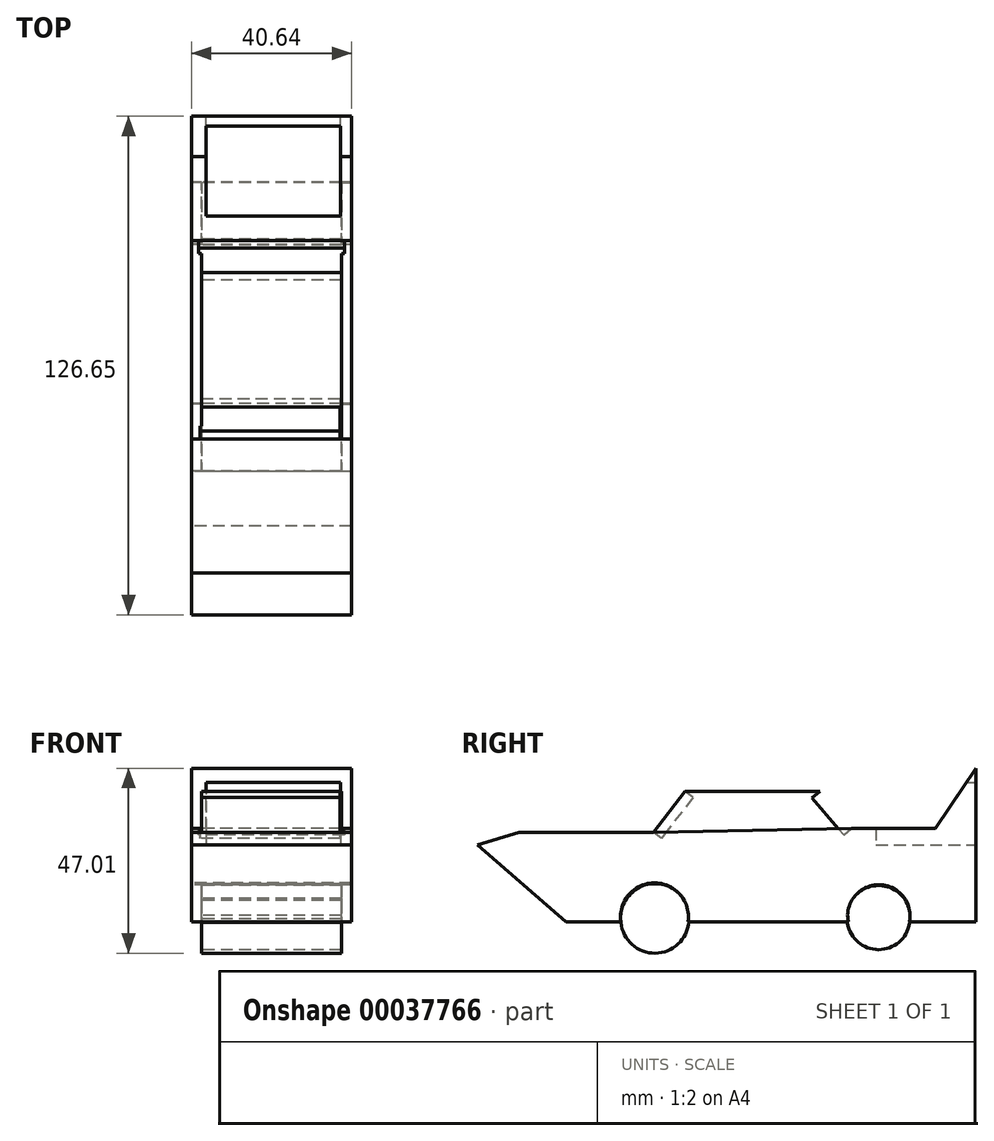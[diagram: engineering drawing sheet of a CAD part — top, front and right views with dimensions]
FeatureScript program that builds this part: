
annotation { "Feature Type Name" : "Feature", "Feature Type Description" : "" }
export const myFeature = defineFeature(function(context is Context, id is Id, definition is map)
    precondition{}
    {
        {
            var Q0;
            Q0=qCreatedBy(makeId("Right.planeOp"),FACE);
            var sketch = newSketch(context, id + "F0", { "sketchPlane" : qUnion([Q0])});
            skLineSegment(sketch, "E0", {"start": v(53.34, 19.52) * mm, "end": v(53.34, -19.52) * mm});
            skLineSegment(sketch, "E1", {"start": v(53.34, -19.52) * mm, "end": v(36.48, -19.52) * mm});
            skArc(sketch, "E2", {"start": v(36.48, -19.52) * mm, "mid": v(28.69, -10.07) * mm, "end": v(20.9, -19.52) * mm});
            skLineSegment(sketch, "E3", {"start": v(20.9, -19.52) * mm, "end": v(-19.8, -19.52) * mm});
            skArc(sketch, "E4", {"start": v(-19.8, -19.52) * mm, "mid": v(-28.32, -9.6) * mm, "end": v(-36.84, -19.52) * mm});
            skLineSegment(sketch, "E5", {"start": v(-36.84, -19.52) * mm, "end": v(-50.75, -19.52) * mm});
            skLineSegment(sketch, "E6", {"start": v(-50.75, -19.52) * mm, "end": v(-73.31, 0) * mm});
            skLineSegment(sketch, "E7", {"start": v(-73.31, 0) * mm, "end": v(-62.74, 3.2) * mm});
            skLineSegment(sketch, "E8", {"start": v(-62.74, 3.2) * mm, "end": v(-28.63, 3.2) * mm});
            skLineSegment(sketch, "E9", {"start": v(-28.63, 3.2) * mm, "end": v(-20.56, 13.66) * mm});
            skLineSegment(sketch, "E10", {"start": v(-20.56, 13.66) * mm, "end": v(13.66, 13.66) * mm});
            skLineSegment(sketch, "E11", {"start": v(13.66, 13.66) * mm, "end": v(21.73, 4.17) * mm});
            skLineSegment(sketch, "E12", {"start": v(21.73, 4.17) * mm, "end": v(43.09, 4.17) * mm});
            skLineSegment(sketch, "E13", {"start": v(43.09, 4.17) * mm, "end": v(53.34, 19.52) * mm});
            skArc(sketch, "E14", {"start": v(20.9, -19.52) * mm, "mid": v(28.69, -25.79) * mm, "end": v(36.48, -19.52) * mm});
            skArc(sketch, "E15", {"start": v(-36.84, -19.52) * mm, "mid": v(-28.32, -26.78) * mm, "end": v(-19.8, -19.52) * mm});
            skLineSegment(sketch, "E16", {"start": v(21.73, 4.17) * mm, "end": v(-28.63, 3.2) * mm});
            skSolve(sketch);
        }
        {
            var Q0;
            Q0=makeQuery(id+"F0.imprint","IMPRINT",FACE,{"disambiguationData":[TD([[makeQuery(id+"F0.imprint","IMPRINT",EDGE,{"derivedFrom":sQuery(id+"F0.wireOp",EDGE,"E9")}),-1.0]])]});
            var Q1;
            Q1=makeQuery(id+"F0.imprint","IMPRINT",FACE,{"disambiguationData":[TD([[makeQuery(id+"F0.imprint","IMPRINT",EDGE,{"derivedFrom":sQuery(id+"F0.wireOp",EDGE,"E0")}),-1.0]])]});
            extrude(context, id + "F1", {"entities" : qUnion([Q0, Q1]), "depth" : 45.72 * mm});
        }
        {
            var Q0;
            Q0=qCreatedBy(makeId("Right.planeOp"),FACE);
            var sketch = newSketch(context, id + "F2", { "sketchPlane" : qUnion([Q0])});
            skArc(sketch, "E17", {"start": v(36.48, -19.89) * mm, "mid": v(28.6, -10.28) * mm, "end": v(20.71, -19.89) * mm});
            skArc(sketch, "E18", {"start": v(20.71, -19.89) * mm, "mid": v(28.6, -26.57) * mm, "end": v(36.48, -19.89) * mm});
            skArc(sketch, "E19", {"start": v(-19.61, -19.52) * mm, "mid": v(-28.33, -9.81) * mm, "end": v(-36.84, -19.7) * mm});
            skArc(sketch, "E20", {"start": v(-36.84, -19.7) * mm, "mid": v(-28.14, -27.49) * mm, "end": v(-19.61, -19.52) * mm});
            skSolve(sketch);
        }
        {
            var Q0;
            Q0=makeQuery(id+"F2.imprint","IMPRINT",FACE,{"disambiguationData":[TD([[makeQuery(id+"F2.imprint","IMPRINT",EDGE,{"derivedFrom":sQuery(id+"F2.wireOp",EDGE,"E17")}),1.0]])]});
            var Q1;
            Q1=makeQuery(id+"F2.imprint","IMPRINT",FACE,{"disambiguationData":[TD([[makeQuery(id+"F2.imprint","IMPRINT",EDGE,{"derivedFrom":sQuery(id+"F2.wireOp",EDGE,"E19")}),1.0]])]});
            extrude(context, id + "F3", {"entities" : qUnion([Q0, Q1]), "operationType" : NewBodyOperationType.ADD, "depth" : 40.64 * mm});
        }
        {
            var Q0;
            Q0=makeQuery(id+"F1.opExtrude","SWEPT_BODY",BODY,{"disambiguationData":[OSD([sQuery(id+"F0.wireOp",EDGE,"E0"),sQuery(id+"F0.wireOp",EDGE,"E1"),sQuery(id+"F0.wireOp",EDGE,"E2"),sQuery(id+"F0.wireOp",EDGE,"E3"),sQuery(id+"F0.wireOp",EDGE,"E4"),sQuery(id+"F0.wireOp",EDGE,"E5"),sQuery(id+"F0.wireOp",EDGE,"E6"),sQuery(id+"F0.wireOp",EDGE,"E7"),sQuery(id+"F0.wireOp",EDGE,"E8"),sQuery(id+"F0.wireOp",EDGE,"E9"),sQuery(id+"F0.wireOp",EDGE,"E10"),sQuery(id+"F0.wireOp",EDGE,"E11"),sQuery(id+"F0.wireOp",EDGE,"E12"),sQuery(id+"F0.wireOp",EDGE,"E13")])]});
            var Q1;
            Q1=qCreatedBy(makeId("Right.planeOp"),FACE);
            mirror(context, id + "F4", {"operationType" : NewBodyOperationType.ADD, "entities" : qUnion([Q0]), "mirrorPlane" : qUnion([Q1])});
        }
        {
            var Q0;
            Q0=makeQuery(id+"F1.opExtrude","CAP_FACE",FACE,{"disambiguationData":[OSD([sQuery(id+"F0.wireOp",EDGE,"E0"),sQuery(id+"F0.wireOp",EDGE,"E1"),sQuery(id+"F0.wireOp",EDGE,"E2"),sQuery(id+"F0.wireOp",EDGE,"E3"),sQuery(id+"F0.wireOp",EDGE,"E4"),sQuery(id+"F0.wireOp",EDGE,"E5"),sQuery(id+"F0.wireOp",EDGE,"E6"),sQuery(id+"F0.wireOp",EDGE,"E7"),sQuery(id+"F0.wireOp",EDGE,"E8"),sQuery(id+"F0.wireOp",EDGE,"E9"),sQuery(id+"F0.wireOp",EDGE,"E10"),sQuery(id+"F0.wireOp",EDGE,"E11"),sQuery(id+"F0.wireOp",EDGE,"E12"),sQuery(id+"F0.wireOp",EDGE,"E13")])],"isStart":false});
            var Q1;
            Q1=makeQuery(id+"F3.opExtrude","CAP_FACE",FACE,{"disambiguationData":[OSD([sQuery(id+"F2.wireOp",EDGE,"E19"),sQuery(id+"F2.wireOp",EDGE,"E20")])],"isStart":false});
            extrude(context, id + "F5", {"entities" : qUnion([Q0, Q1]), "operationType" : NewBodyOperationType.REMOVE, "oppositeDirection" : true, "depth" : 25.4 * mm});
        }
        {
            var Q0;
            Q0=makeQuery(id+"F3.opExtrude","CAP_FACE",FACE,{"disambiguationData":[OSD([sQuery(id+"F2.wireOp",EDGE,"E17"),sQuery(id+"F2.wireOp",EDGE,"E18")])],"isStart":false});
            extrude(context, id + "F6", {"entities" : qUnion([Q0]), "operationType" : NewBodyOperationType.REMOVE, "oppositeDirection" : true, "depth" : 25.4 * mm});
        }
        {
            var Q0;
            Q0=makeQuery(id+"F4.opPattern","COPY",FACE,{"derivedFrom":makeQuery(id+"F1.opExtrude","CAP_FACE",FACE,{"disambiguationData":[OSD([sQuery(id+"F0.wireOp",EDGE,"E0"),sQuery(id+"F0.wireOp",EDGE,"E1"),sQuery(id+"F0.wireOp",EDGE,"E2"),sQuery(id+"F0.wireOp",EDGE,"E3"),sQuery(id+"F0.wireOp",EDGE,"E4"),sQuery(id+"F0.wireOp",EDGE,"E5"),sQuery(id+"F0.wireOp",EDGE,"E6"),sQuery(id+"F0.wireOp",EDGE,"E7"),sQuery(id+"F0.wireOp",EDGE,"E8"),sQuery(id+"F0.wireOp",EDGE,"E9"),sQuery(id+"F0.wireOp",EDGE,"E10"),sQuery(id+"F0.wireOp",EDGE,"E11"),sQuery(id+"F0.wireOp",EDGE,"E12"),sQuery(id+"F0.wireOp",EDGE,"E13")])],"isStart":false}),"instanceName":"1"});
            extrude(context, id + "F7", {"entities" : qUnion([Q0]), "operationType" : NewBodyOperationType.REMOVE, "oppositeDirection" : true, "depth" : 25.4 * mm});
        }
        {
            var Q0;
            Q0=makeQuery(id+"F4.opPattern","COPY",FACE,{"derivedFrom":makeQuery(id+"F3.opExtrude","CAP_FACE",FACE,{"disambiguationData":[OSD([sQuery(id+"F2.wireOp",EDGE,"E17"),sQuery(id+"F2.wireOp",EDGE,"E18")])],"isStart":false}),"instanceName":"1"});
            var Q1;
            Q1=makeQuery(id+"F4.opPattern","COPY",FACE,{"derivedFrom":makeQuery(id+"F3.opExtrude","CAP_FACE",FACE,{"disambiguationData":[OSD([sQuery(id+"F2.wireOp",EDGE,"E19"),sQuery(id+"F2.wireOp",EDGE,"E20")])],"isStart":false}),"instanceName":"1"});
            extrude(context, id + "F8", {"entities" : qUnion([Q0, Q1]), "operationType" : NewBodyOperationType.REMOVE, "oppositeDirection" : true, "depth" : 25.4 * mm});
        }
        {
            var Q0;
            Q0=makeQuery(id+"F5.boolean.opBoolean","COPY",FACE,{"derivedFrom":makeQuery(id+"F5.opExtrude","CAP_FACE",FACE,{"disambiguationData":[OSD([sQuery(id+"F2.wireOp",EDGE,"E19"),sQuery(id+"F2.wireOp",EDGE,"E20")])],"isStart":false})});
            var Q1;
            Q1=makeQuery(id+"F6.boolean.opBoolean","COPY",FACE,{"derivedFrom":makeQuery(id+"F6.opExtrude","CAP_FACE",FACE,{"disambiguationData":[OSD([sQuery(id+"F2.wireOp",EDGE,"E17"),sQuery(id+"F2.wireOp",EDGE,"E18")])],"isStart":false})});
            extrude(context, id + "F9", {"entities" : qUnion([Q0, Q1]), "operationType" : NewBodyOperationType.ADD, "depth" : 2.54 * mm});
        }
        {
            var Q0;
            Q0=makeQuery(id+"F8.boolean.opBoolean","COPY",FACE,{"derivedFrom":makeQuery(id+"F8.opExtrude","CAP_FACE",FACE,{"disambiguationData":[OSD([sQuery(id+"F2.wireOp",EDGE,"E17"),sQuery(id+"F2.wireOp",EDGE,"E18")])],"isStart":false})});
            var Q1;
            Q1=makeQuery(id+"F8.boolean.opBoolean","COPY",FACE,{"derivedFrom":makeQuery(id+"F8.opExtrude","CAP_FACE",FACE,{"disambiguationData":[OSD([sQuery(id+"F2.wireOp",EDGE,"E19"),sQuery(id+"F2.wireOp",EDGE,"E20")])],"isStart":false})});
            extrude(context, id + "F10", {"entities" : qUnion([Q0, Q1]), "operationType" : NewBodyOperationType.ADD, "depth" : 2.54 * mm});
        }
        {
            var Q0;
            {var subQ0=makeQuery(id+"F1.opExtrude","SWEPT_FACE",FACE,{"disambiguationData":[OSD([sQuery(id+"F0.wireOp",EDGE,"E9")])]});Q0=makeQuery(id+"F4.boolean.opBoolean","MERGE",FACE,{"derivedFrom":[subQ0,makeQuery(id+"F4.opPattern","COPY",FACE,{"derivedFrom":subQ0,"instanceName":"1"})]});}
            var sketch = newSketch(context, id + "F11", { "sketchPlane" : qUnion([Q0])});
            skLineSegment(sketch, "E21.bottom", {"start": v(-18.15, -1.74) * mm, "end": v(17.41, -1.74) * mm});
            skLineSegment(sketch, "E21.top", {"start": v(-18.15, -14.95) * mm, "end": v(17.41, -14.95) * mm});
            skLineSegment(sketch, "E21.left", {"start": v(-18.15, -1.74) * mm, "end": v(-18.15, -14.95) * mm});
            skLineSegment(sketch, "E21.right", {"start": v(17.41, -1.74) * mm, "end": v(17.41, -14.95) * mm});
            skSolve(sketch);
        }
        {
            var Q0;
            Q0=makeQuery(id+"F11.imprint","IMPRINT",FACE,{"disambiguationData":[TD([[makeQuery(id+"F11.imprint","IMPRINT",EDGE,{"derivedFrom":sQuery(id+"F11.wireOp",EDGE,"E21.bottom")}),1.0]])]});
            extrude(context, id + "F12", {"entities" : qUnion([Q0]), "operationType" : NewBodyOperationType.REMOVE, "oppositeDirection" : true, "depth" : 2.54 * mm});
        }
        {
            var Q0;
            {var subQ0=makeQuery(id+"F1.opExtrude","SWEPT_FACE",FACE,{"disambiguationData":[OSD([sQuery(id+"F0.wireOp",EDGE,"E11")])]});Q0=makeQuery(id+"F4.boolean.opBoolean","MERGE",FACE,{"derivedFrom":[subQ0,makeQuery(id+"F4.opPattern","COPY",FACE,{"derivedFrom":subQ0,"instanceName":"1"})]});}
            var sketch = newSketch(context, id + "F13", { "sketchPlane" : qUnion([Q0])});
            skLineSegment(sketch, "E22.bottom", {"start": v(-18.51, 1.55) * mm, "end": v(18.51, 1.55) * mm});
            skLineSegment(sketch, "E22.top", {"start": v(-18.51, -10.9) * mm, "end": v(18.51, -10.9) * mm});
            skLineSegment(sketch, "E22.left", {"start": v(-18.51, 1.55) * mm, "end": v(-18.51, -10.9) * mm});
            skLineSegment(sketch, "E22.right", {"start": v(18.51, 1.55) * mm, "end": v(18.51, -10.9) * mm});
            skSolve(sketch);
        }
        {
            var Q0;
            Q0=makeQuery(id+"F13.imprint","IMPRINT",FACE,{"disambiguationData":[TD([[makeQuery(id+"F13.imprint","IMPRINT",EDGE,{"derivedFrom":sQuery(id+"F13.wireOp",EDGE,"E22.bottom")}),-1.0]])]});
            extrude(context, id + "F14", {"entities" : qUnion([Q0]), "operationType" : NewBodyOperationType.REMOVE, "oppositeDirection" : true, "depth" : 2.54 * mm});
        }
        {
            var Q0;
            Q0=makeQuery(id+"F5.boolean.opBoolean","COPY",FACE,{"derivedFrom":makeQuery(id+"F5.opExtrude","CAP_FACE",FACE,{"disambiguationData":[OSD([sQuery(id+"F0.wireOp",EDGE,"E0"),sQuery(id+"F0.wireOp",EDGE,"E1"),sQuery(id+"F0.wireOp",EDGE,"E2"),sQuery(id+"F0.wireOp",EDGE,"E3"),sQuery(id+"F0.wireOp",EDGE,"E4"),sQuery(id+"F0.wireOp",EDGE,"E5"),sQuery(id+"F0.wireOp",EDGE,"E6"),sQuery(id+"F0.wireOp",EDGE,"E7"),sQuery(id+"F0.wireOp",EDGE,"E8"),sQuery(id+"F0.wireOp",EDGE,"E9"),sQuery(id+"F0.wireOp",EDGE,"E10"),sQuery(id+"F0.wireOp",EDGE,"E11"),sQuery(id+"F0.wireOp",EDGE,"E12"),sQuery(id+"F0.wireOp",EDGE,"E13")])],"isStart":false})});
            var sketch = newSketch(context, id + "F15", { "sketchPlane" : qUnion([Q0])});
            skLineSegment(sketch, "E23", {"start": v(-28.63, 3.2) * mm, "end": v(21.73, 4.17) * mm});
            skLineSegment(sketch, "E24", {"start": v(21.73, 4.17) * mm, "end": v(13.66, 13.66) * mm});
            skLineSegment(sketch, "E25", {"start": v(13.66, 13.66) * mm, "end": v(-20.56, 13.66) * mm});
            skLineSegment(sketch, "E26", {"start": v(-20.56, 13.66) * mm, "end": v(-28.63, 3.2) * mm});
            skSolve(sketch);
        }
        {
            var Q0;
            Q0=makeQuery(id+"F7.boolean.opBoolean","COPY",FACE,{"derivedFrom":makeQuery(id+"F7.opExtrude","CAP_FACE",FACE,{"disambiguationData":[OSD([sQuery(id+"F0.wireOp",EDGE,"E0"),sQuery(id+"F0.wireOp",EDGE,"E1"),sQuery(id+"F0.wireOp",EDGE,"E2"),sQuery(id+"F0.wireOp",EDGE,"E3"),sQuery(id+"F0.wireOp",EDGE,"E4"),sQuery(id+"F0.wireOp",EDGE,"E5"),sQuery(id+"F0.wireOp",EDGE,"E6"),sQuery(id+"F0.wireOp",EDGE,"E7"),sQuery(id+"F0.wireOp",EDGE,"E8"),sQuery(id+"F0.wireOp",EDGE,"E9"),sQuery(id+"F0.wireOp",EDGE,"E10"),sQuery(id+"F0.wireOp",EDGE,"E11"),sQuery(id+"F0.wireOp",EDGE,"E12"),sQuery(id+"F0.wireOp",EDGE,"E13")])],"isStart":false})});
            var sketch = newSketch(context, id + "F16", { "sketchPlane" : qUnion([Q0])});
            skLineSegment(sketch, "E27", {"start": v(-21.73, 4.17) * mm, "end": v(-13.66, 13.66) * mm});
            skLineSegment(sketch, "E28", {"start": v(-13.66, 13.66) * mm, "end": v(20.56, 13.66) * mm});
            skLineSegment(sketch, "E29", {"start": v(20.56, 13.66) * mm, "end": v(28.63, 3.2) * mm});
            skLineSegment(sketch, "E30", {"start": v(28.63, 3.2) * mm, "end": v(-21.73, 4.17) * mm});
            skSolve(sketch);
        }
        {
            var Q0;
            Q0=makeQuery(id+"F16.imprint","IMPRINT",FACE,{"disambiguationData":[TD([[makeQuery(id+"F16.imprint","IMPRINT",EDGE,{"derivedFrom":sQuery(id+"F16.wireOp",EDGE,"E27")}),1.0]])]});
            extrude(context, id + "F17", {"entities" : qUnion([Q0]), "operationType" : NewBodyOperationType.REMOVE, "oppositeDirection" : true, "depth" : 2.54 * mm});
        }
        {
            var Q0;
            Q0=makeQuery(id+"F15.imprint","IMPRINT",FACE,{"disambiguationData":[TD([[makeQuery(id+"F15.imprint","IMPRINT",EDGE,{"derivedFrom":sQuery(id+"F15.wireOp",EDGE,"E23")}),1.0]])]});
            extrude(context, id + "F18", {"entities" : qUnion([Q0]), "operationType" : NewBodyOperationType.REMOVE, "oppositeDirection" : true, "depth" : 2.54 * mm});
        }
        {
            var Q0;
            {var subQ0=makeQuery(id+"F1.opExtrude","SWEPT_FACE",FACE,{"disambiguationData":[OSD([sQuery(id+"F0.wireOp",EDGE,"E0")])]});Q0=makeQuery(id+"F4.boolean.opBoolean","MERGE",FACE,{"derivedFrom":[subQ0,makeQuery(id+"F4.opPattern","COPY",FACE,{"derivedFrom":subQ0,"instanceName":"1"})]});}
            var sketch = newSketch(context, id + "F19", { "sketchPlane" : qUnion([Q0])});
            skLineSegment(sketch, "E31.bottom", {"start": v(-17.6, 15.86) * mm, "end": v(16.68, 15.86) * mm});
            skLineSegment(sketch, "E31.top", {"start": v(-17.6, 0) * mm, "end": v(16.68, 0) * mm});
            skLineSegment(sketch, "E31.left", {"start": v(-17.6, 15.86) * mm, "end": v(-17.6, 0) * mm});
            skLineSegment(sketch, "E31.right", {"start": v(16.68, 15.86) * mm, "end": v(16.68, 0) * mm});
            skSolve(sketch);
        }
        {
            var Q0;
            Q0=makeQuery(id+"F19.imprint","IMPRINT",FACE,{"disambiguationData":[TD([[makeQuery(id+"F19.imprint","IMPRINT",EDGE,{"derivedFrom":sQuery(id+"F19.wireOp",EDGE,"E31.bottom")}),-1.0]])]});
            extrude(context, id + "F20", {"entities" : qUnion([Q0]), "operationType" : NewBodyOperationType.REMOVE, "oppositeDirection" : true, "depth" : 25.4 * mm});
        }
    });
